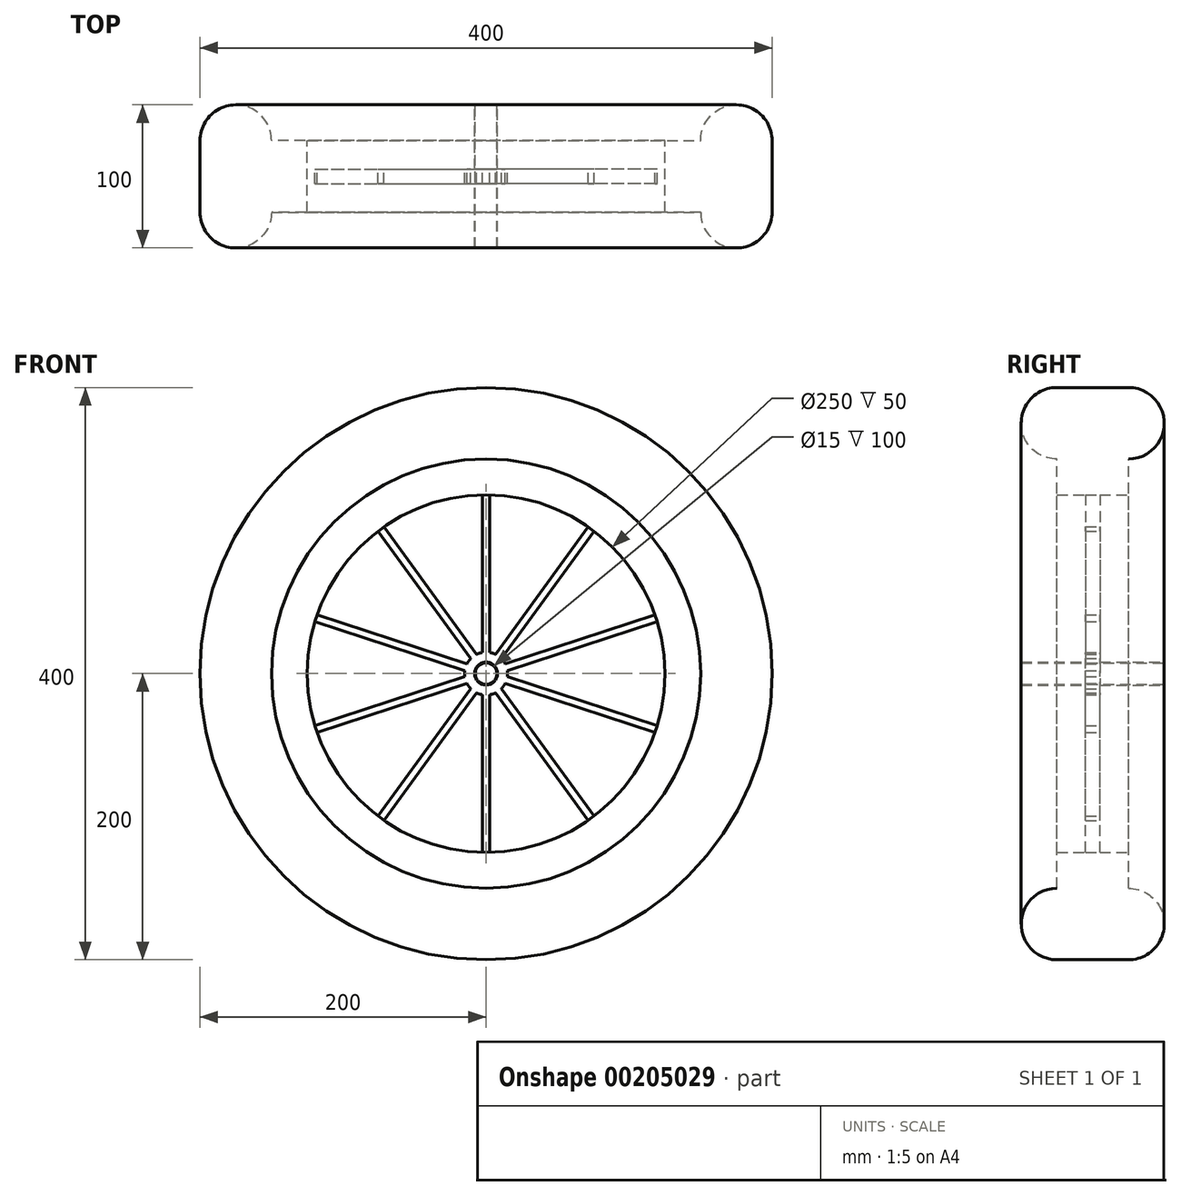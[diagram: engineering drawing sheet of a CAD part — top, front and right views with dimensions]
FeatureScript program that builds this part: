
annotation { "Feature Type Name" : "Feature", "Feature Type Description" : "" }
export const myFeature = defineFeature(function(context is Context, id is Id, definition is map)
    precondition{}
    {
        {
            var Q0;
            Q0=qCreatedBy(makeId("Front.planeOp"),FACE);
            var sketch = newSketch(context, id + "F0", { "sketchPlane" : qUnion([Q0])});
            skCircle(sketch, "E0", {"center": v(0, 0) * mm, "radius": 150 * mm});
            skCircle(sketch, "E1", {"center": v(0, 0) * mm, "radius": 125 * mm});
            skSolve(sketch);
        }
        {
            var Q0;
            Q0 = qSketchRegion(id + "F0", true);
            extrude(context, id + "F1", {"entities" : qUnion([Q0]), "depth" : 25 * mm});
        }
        {
            var Q0;
            Q0=qCreatedBy(makeId("Front.planeOp"),FACE);
            var sketch = newSketch(context, id + "F2", { "sketchPlane" : qUnion([Q0])});
            skCircle(sketch, "E2", {"center": v(0, 0) * mm, "radius": 150 * mm});
            skCircle(sketch, "E3", {"center": v(0, 0) * mm, "radius": 200 * mm});
            skSolve(sketch);
        }
        {
            var Q0;
            Q0 = qSketchRegion(id + "F2", true);
            extrude(context, id + "F3", {"entities" : qUnion([Q0]), "operationType" : NewBodyOperationType.ADD, "depth" : 50 * mm});
        }
        {
            var Q0;
            Q0=makeQuery(id+"F1.opExtrude","SWEPT_BODY",BODY,{"disambiguationData":[OSD([sQuery(id+"F0.wireOp",EDGE,"E0"),sQuery(id+"F0.wireOp",EDGE,"E1")])]});
            var Q1;
            Q1=makeQuery(id+"F3.boolean.opBoolean","MERGE",FACE,{"derivedFrom":[makeQuery(id+"F1.opExtrude","CAP_FACE",FACE,{"disambiguationData":[OSD([sQuery(id+"F0.wireOp",EDGE,"E0"),sQuery(id+"F0.wireOp",EDGE,"E1")])],"isStart":true}),makeQuery(id+"F3.opExtrude","CAP_FACE",FACE,{"disambiguationData":[OSD([sQuery(id+"F2.wireOp",EDGE,"E2"),sQuery(id+"F2.wireOp",EDGE,"E3")])],"isStart":true})]});
            mirror(context, id + "F4", {"operationType" : NewBodyOperationType.ADD, "entities" : qUnion([Q0]), "mirrorPlane" : qUnion([Q1])});
        }
        {
            var Q0;
            Q0=makeQuery(id+"F3.opExtrude","CAP_FACE",FACE,{"disambiguationData":[OSD([sQuery(id+"F2.wireOp",EDGE,"E2"),sQuery(id+"F2.wireOp",EDGE,"E3")])],"isStart":false});
            var Q1;
            Q1=makeQuery(id+"F4.opPattern","COPY",FACE,{"derivedFrom":makeQuery(id+"F3.opExtrude","CAP_FACE",FACE,{"disambiguationData":[OSD([sQuery(id+"F2.wireOp",EDGE,"E2"),sQuery(id+"F2.wireOp",EDGE,"E3")])],"isStart":false}),"instanceName":"1"});
            fillet(context, id + "F5", {"entities" : qUnion([Q0, Q1]), "radius" : 25 * mm, "tangentPropagation" : true, "allowEdgeOverflow" : false});
        }
        {
            var Q0;
            Q0=qCreatedBy(makeId("Front.planeOp"),FACE);
            var sketch = newSketch(context, id + "F6", { "sketchPlane" : qUnion([Q0])});
            skCircle(sketch, "E4", {"center": v(0, 0) * mm, "radius": 15 * mm});
            skLineSegment(sketch, "E5", {"start": v(0, 0) * mm, "end": v(0, 15) * mm, "construction": true});
            skLineSegment(sketch, "E6", {"start": v(0, 165) * mm, "end": v(-2.5, 165) * mm});
            skLineSegment(sketch, "E7", {"start": v(-2.5, 165) * mm, "end": v(-2.5, 14.8) * mm});
            skLineSegment(sketch, "E8", {"start": v(0, 15) * mm, "end": v(0, 165) * mm, "construction": true});
            skLineSegment(sketch, "E9.MirrorCS", {"start": v(0, 165) * mm, "end": v(2.5, 165) * mm});
            skLineSegment(sketch, "E10.MirrorCS", {"start": v(2.5, 165) * mm, "end": v(2.5, 14.8) * mm});
            skLineSegment(sketch, "E11.1.0", {"start": v(-99, 132.02) * mm, "end": v(-10.72, 10.5) * mm});
            skLineSegment(sketch, "E11.1.1", {"start": v(-96.98, 133.49) * mm, "end": v(-99, 132.02) * mm});
            skLineSegment(sketch, "E11.1.2", {"start": v(-96.98, 133.49) * mm, "end": v(-94.96, 134.96) * mm});
            skLineSegment(sketch, "E11.1.3", {"start": v(-94.96, 134.96) * mm, "end": v(-6.67, 13.43) * mm});
            skLineSegment(sketch, "E11.2.0", {"start": v(-157.7, 48.61) * mm, "end": v(-14.84, 2.2) * mm});
            skLineSegment(sketch, "E11.2.1", {"start": v(-156.92, 50.99) * mm, "end": v(-157.7, 48.61) * mm});
            skLineSegment(sketch, "E11.2.2", {"start": v(-156.92, 50.99) * mm, "end": v(-156.15, 53.37) * mm});
            skLineSegment(sketch, "E11.2.3", {"start": v(-156.15, 53.37) * mm, "end": v(-13.3, 6.95) * mm});
            skLineSegment(sketch, "E11.3.0", {"start": v(-156.15, -53.37) * mm, "end": v(-13.3, -6.95) * mm});
            skLineSegment(sketch, "E11.3.1", {"start": v(-156.92, -50.99) * mm, "end": v(-156.15, -53.37) * mm});
            skLineSegment(sketch, "E11.3.2", {"start": v(-156.92, -50.99) * mm, "end": v(-157.7, -48.61) * mm});
            skLineSegment(sketch, "E11.3.3", {"start": v(-157.7, -48.61) * mm, "end": v(-14.84, -2.2) * mm});
            skLineSegment(sketch, "E11.4.0", {"start": v(-94.96, -134.96) * mm, "end": v(-6.67, -13.43) * mm});
            skLineSegment(sketch, "E11.4.1", {"start": v(-96.98, -133.49) * mm, "end": v(-94.96, -134.96) * mm});
            skLineSegment(sketch, "E11.4.2", {"start": v(-96.98, -133.49) * mm, "end": v(-99, -132.02) * mm});
            skLineSegment(sketch, "E11.4.3", {"start": v(-99, -132.02) * mm, "end": v(-10.72, -10.5) * mm});
            skLineSegment(sketch, "E11.5.0", {"start": v(2.5, -165) * mm, "end": v(2.5, -14.8) * mm});
            skLineSegment(sketch, "E11.5.1", {"start": v(0, -165) * mm, "end": v(2.5, -165) * mm});
            skLineSegment(sketch, "E11.5.2", {"start": v(0, -165) * mm, "end": v(-2.5, -165) * mm});
            skLineSegment(sketch, "E11.5.3", {"start": v(-2.5, -165) * mm, "end": v(-2.5, -14.8) * mm});
            skLineSegment(sketch, "E11.6.0", {"start": v(99, -132.02) * mm, "end": v(10.72, -10.5) * mm});
            skLineSegment(sketch, "E11.6.1", {"start": v(96.98, -133.49) * mm, "end": v(99, -132.02) * mm});
            skLineSegment(sketch, "E11.6.2", {"start": v(96.98, -133.49) * mm, "end": v(94.96, -134.96) * mm});
            skLineSegment(sketch, "E11.6.3", {"start": v(94.96, -134.96) * mm, "end": v(6.67, -13.43) * mm});
            skLineSegment(sketch, "E11.7.0", {"start": v(157.7, -48.61) * mm, "end": v(14.84, -2.2) * mm});
            skLineSegment(sketch, "E11.7.1", {"start": v(156.92, -50.99) * mm, "end": v(157.7, -48.61) * mm});
            skLineSegment(sketch, "E11.7.2", {"start": v(156.92, -50.99) * mm, "end": v(156.15, -53.37) * mm});
            skLineSegment(sketch, "E11.7.3", {"start": v(156.15, -53.37) * mm, "end": v(13.3, -6.95) * mm});
            skLineSegment(sketch, "E11.8.0", {"start": v(156.15, 53.37) * mm, "end": v(13.3, 6.95) * mm});
            skLineSegment(sketch, "E11.8.1", {"start": v(156.92, 50.99) * mm, "end": v(156.15, 53.37) * mm});
            skLineSegment(sketch, "E11.8.2", {"start": v(156.92, 50.99) * mm, "end": v(157.7, 48.61) * mm});
            skLineSegment(sketch, "E11.8.3", {"start": v(157.7, 48.61) * mm, "end": v(14.84, 2.2) * mm});
            skLineSegment(sketch, "E11.9.0", {"start": v(94.96, 134.96) * mm, "end": v(6.67, 13.43) * mm});
            skLineSegment(sketch, "E11.9.1", {"start": v(96.98, 133.49) * mm, "end": v(94.96, 134.96) * mm});
            skLineSegment(sketch, "E11.9.2", {"start": v(96.98, 133.49) * mm, "end": v(99, 132.02) * mm});
            skLineSegment(sketch, "E11.9.3", {"start": v(99, 132.02) * mm, "end": v(10.72, 10.5) * mm});
            skSolve(sketch);
        }
        {
            var Q0;
            Q0 = qSketchRegion(id + "F6", true);
            extrude(context, id + "F7", {"entities" : qUnion([Q0]), "operationType" : NewBodyOperationType.ADD, "depth" : 5 * mm});
        }
        {
            var Q0;
            Q0=makeQuery(id+"F1.opExtrude","SWEPT_BODY",BODY,{"disambiguationData":[OSD([sQuery(id+"F0.wireOp",EDGE,"E0"),sQuery(id+"F0.wireOp",EDGE,"E1")])]});
            var Q1;
            Q1=makeQuery(id+"F7.opExtrude","CAP_FACE",FACE,{"disambiguationData":[OSD([sQuery(id+"F6.wireOp",EDGE,"E4"),sQuery(id+"F6.wireOp",EDGE,"E6"),sQuery(id+"F6.wireOp",EDGE,"E7"),sQuery(id+"F6.wireOp",EDGE,"E9.MirrorCS"),sQuery(id+"F6.wireOp",EDGE,"E10.MirrorCS"),sQuery(id+"F6.wireOp",EDGE,"E11.1.0"),sQuery(id+"F6.wireOp",EDGE,"E11.1.1"),sQuery(id+"F6.wireOp",EDGE,"E11.1.2"),sQuery(id+"F6.wireOp",EDGE,"E11.1.3"),sQuery(id+"F6.wireOp",EDGE,"E11.2.0"),sQuery(id+"F6.wireOp",EDGE,"E11.2.1"),sQuery(id+"F6.wireOp",EDGE,"E11.2.2"),sQuery(id+"F6.wireOp",EDGE,"E11.2.3"),sQuery(id+"F6.wireOp",EDGE,"E11.3.0"),sQuery(id+"F6.wireOp",EDGE,"E11.3.1"),sQuery(id+"F6.wireOp",EDGE,"E11.3.2"),sQuery(id+"F6.wireOp",EDGE,"E11.3.3"),sQuery(id+"F6.wireOp",EDGE,"E11.4.0"),sQuery(id+"F6.wireOp",EDGE,"E11.4.1"),sQuery(id+"F6.wireOp",EDGE,"E11.4.2"),sQuery(id+"F6.wireOp",EDGE,"E11.4.3"),sQuery(id+"F6.wireOp",EDGE,"E11.5.0"),sQuery(id+"F6.wireOp",EDGE,"E11.5.1"),sQuery(id+"F6.wireOp",EDGE,"E11.5.2"),sQuery(id+"F6.wireOp",EDGE,"E11.5.3"),sQuery(id+"F6.wireOp",EDGE,"E11.6.0"),sQuery(id+"F6.wireOp",EDGE,"E11.6.1"),sQuery(id+"F6.wireOp",EDGE,"E11.6.2"),sQuery(id+"F6.wireOp",EDGE,"E11.6.3"),sQuery(id+"F6.wireOp",EDGE,"E11.7.0"),sQuery(id+"F6.wireOp",EDGE,"E11.7.1"),sQuery(id+"F6.wireOp",EDGE,"E11.7.2"),sQuery(id+"F6.wireOp",EDGE,"E11.7.3"),sQuery(id+"F6.wireOp",EDGE,"E11.8.0"),sQuery(id+"F6.wireOp",EDGE,"E11.8.1"),sQuery(id+"F6.wireOp",EDGE,"E11.8.2"),sQuery(id+"F6.wireOp",EDGE,"E11.8.3"),sQuery(id+"F6.wireOp",EDGE,"E11.9.0"),sQuery(id+"F6.wireOp",EDGE,"E11.9.1"),sQuery(id+"F6.wireOp",EDGE,"E11.9.2"),sQuery(id+"F6.wireOp",EDGE,"E11.9.3")])],"isStart":true});
            mirror(context, id + "F8", {"operationType" : NewBodyOperationType.ADD, "entities" : qUnion([Q0]), "mirrorPlane" : qUnion([Q1])});
        }
        {
            var Q0;
            Q0=qCreatedBy(makeId("Front.planeOp"),FACE);
            var sketch = newSketch(context, id + "F9", { "sketchPlane" : qUnion([Q0])});
            skCircle(sketch, "E12", {"center": v(0, 0) * mm, "radius": 8 * mm});
            skSolve(sketch);
        }
        {
            var Q0;
            Q0 = qSketchRegion(id + "F9", true);
            extrude(context, id + "F10", {"entities" : qUnion([Q0]), "depth" : 50 * mm});
        }
        {
            var Q0;
            Q0=qCreatedBy(makeId("Front.planeOp"),FACE);
            var sketch = newSketch(context, id + "F11", { "sketchPlane" : qUnion([Q0])});
            skCircle(sketch, "E13", {"center": v(0, 0) * mm, "radius": 5 * mm});
            skSolve(sketch);
        }
        {
            var Q0;
            Q0 = qSketchRegion(id + "F11", true);
            extrude(context, id + "F12", {"entities" : qUnion([Q0]), "operationType" : NewBodyOperationType.REMOVE, "endBound" : BoundingType.THROUGH_ALL, "depth" : 120 * mm});
        }
        {
            var Q0;
            Q0=makeQuery(id+"F10.opExtrude","SWEPT_BODY",BODY,{"disambiguationData":[OSD([sQuery(id+"F9.wireOp",EDGE,"E12")])]});
            var Q1;
            Q1=makeQuery(id+"F10.opExtrude","CAP_FACE",FACE,{"disambiguationData":[OSD([sQuery(id+"F9.wireOp",EDGE,"E12")])],"isStart":true});
            mirror(context, id + "F13", {"operationType" : NewBodyOperationType.ADD, "entities" : qUnion([Q0]), "mirrorPlane" : qUnion([Q1])});
        }
        {
            var Q0;
            Q0=qCreatedBy(makeId("Front.planeOp"),FACE);
            var sketch = newSketch(context, id + "F14", { "sketchPlane" : qUnion([Q0])});
            skCircle(sketch, "E14", {"center": v(0, 0) * mm, "radius": 7.5 * mm});
            skSolve(sketch);
        }
        {
            var Q0;
            Q0 = qSketchRegion(id + "F14", true);
            extrude(context, id + "F15", {"entities" : qUnion([Q0]), "depth" : 100 * mm});
        }
        {
            var Q0;
            Q0=makeQuery(id+"F15.opExtrude","SWEPT_BODY",BODY,{"disambiguationData":[OSD([sQuery(id+"F14.wireOp",EDGE,"E14")])]});
            var Q1;
            Q1=qCreatedBy(makeId("Front.planeOp"),FACE);
            mirror(context, id + "F16", {"operationType" : NewBodyOperationType.ADD, "entities" : qUnion([Q0]), "mirrorPlane" : qUnion([Q1])});
        }
        {
            var Q0;
            Q0=qCreatedBy(makeId("Front.planeOp"),FACE);
            var sketch = newSketch(context, id + "F17", { "sketchPlane" : qUnion([Q0])});
            skCircle(sketch, "E15", {"center": v(0, 0) * mm, "radius": 7.5 * mm});
            skSolve(sketch);
        }
        {
            var Q0;
            Q0 = qSketchRegion(id + "F17", true);
            extrude(context, id + "F18", {"entities" : qUnion([Q0]), "operationType" : NewBodyOperationType.REMOVE, "endBound" : BoundingType.UP_TO_NEXT, "depth" : 25 * mm, "hasSecondDirection" : true, "secondDirectionBound" : SecondDirectionBoundingType.UP_TO_NEXT, "secondDirectionOppositeDirection" : true, "secondDirectionDepth" : 25 * mm});
        }
    });
